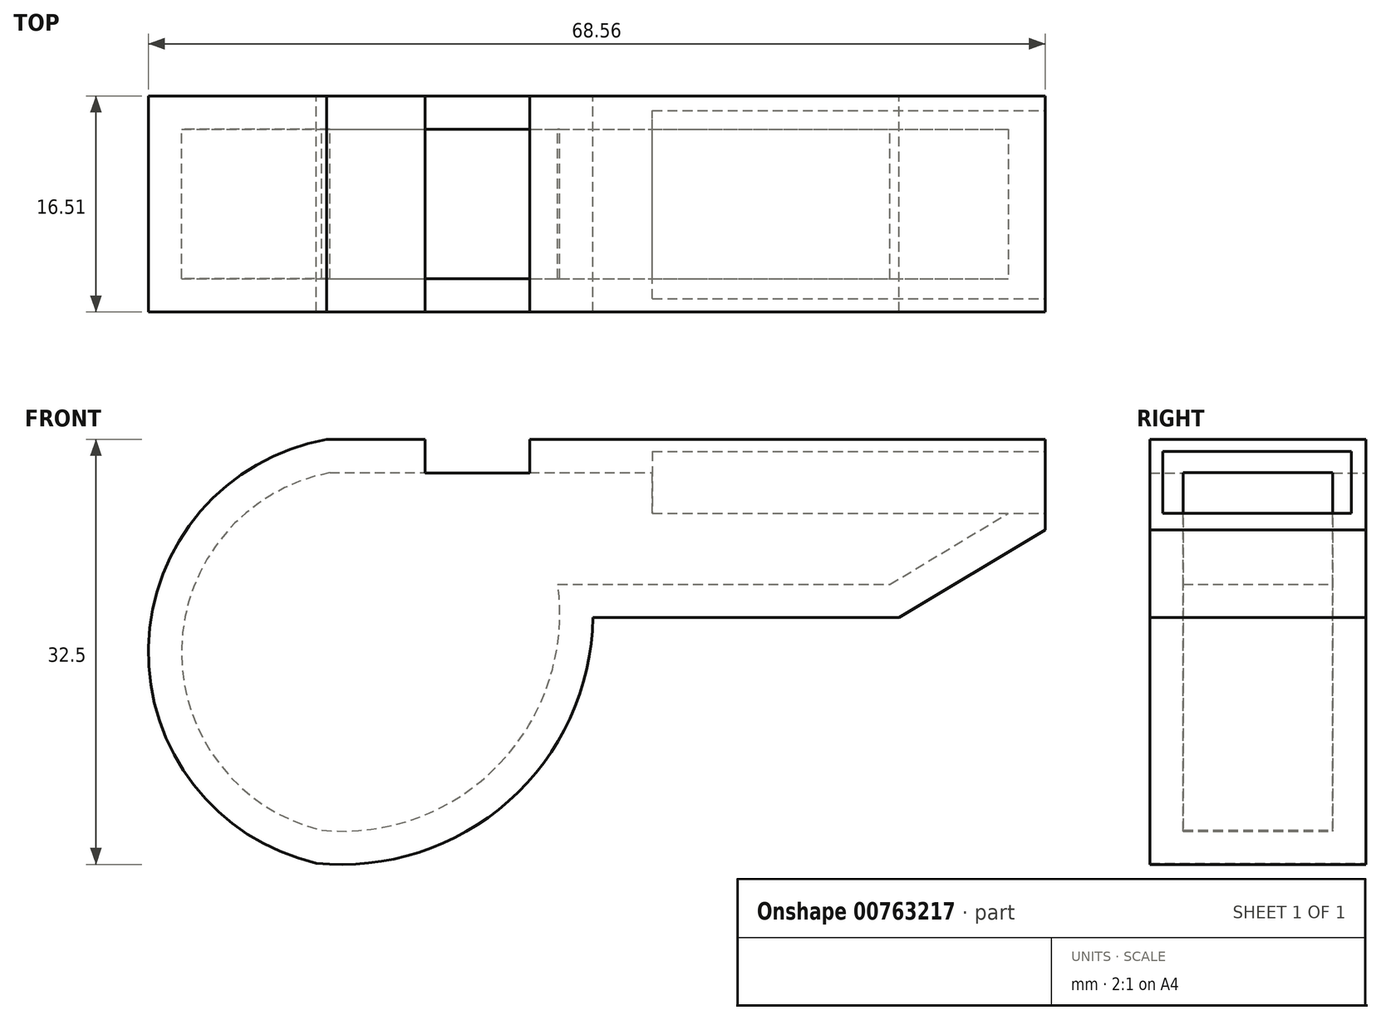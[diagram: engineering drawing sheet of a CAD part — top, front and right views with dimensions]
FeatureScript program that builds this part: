
annotation { "Feature Type Name" : "Feature", "Feature Type Description" : "" }
export const myFeature = defineFeature(function(context is Context, id is Id, definition is map)
    precondition{}
    {
        {
            var Q0;
            Q0=qCreatedBy(makeId("Front.planeOp"),FACE);
            var sketch = newSketch(context, id + "F0", { "sketchPlane" : qUnion([Q0])});
            skArc(sketch, "E0", {"start": v(-7.5, 23.6) * mm, "mid": v(-21.14, 7.73) * mm, "end": v(-8.3, -8.8) * mm});
            skLineSegment(sketch, "E1", {"start": v(-4.6, 23.6) * mm, "end": v(-7.5, 23.6) * mm});
            skLineSegment(sketch, "E2", {"start": v(-4.6, 23.6) * mm, "end": v(47.41, 23.6) * mm});
            skLineSegment(sketch, "E3", {"start": v(47.41, 23.6) * mm, "end": v(47.41, 16.7) * mm});
            skLineSegment(sketch, "E4", {"start": v(47.41, 16.7) * mm, "end": v(47.41, 9.98) * mm});
            skArc(sketch, "E5", {"start": v(-8.3, -8.8) * mm, "mid": v(6.4, -4.06) * mm, "end": v(12.84, 9.98) * mm});
            skLineSegment(sketch, "E6", {"start": v(12.84, 9.98) * mm, "end": v(36.23, 9.98) * mm});
            skLineSegment(sketch, "E7", {"start": v(36.23, 9.98) * mm, "end": v(47.41, 16.7) * mm});
            skSolve(sketch);
        }
        {
            var Q0;
            Q0=makeQuery(id+"F0.imprint","IMPRINT",FACE,{"disambiguationData":[TD([[makeQuery(id+"F0.imprint","IMPRINT",EDGE,{"derivedFrom":sQuery(id+"F0.wireOp",EDGE,"E0")}),1.0]])]});
            extrude(context, id + "F1", {"entities" : qUnion([Q0]), "depth" : 16.5 * mm, "offsetDistance" : 25.4 * mm});
        }
        {
            var Q0;
            Q0=makeQuery(id+"F1.opExtrude","CAP_FACE",FACE,{"disambiguationData":[OSD([sQuery(id+"F0.wireOp",EDGE,"E0"),sQuery(id+"F0.wireOp",EDGE,"E1"),sQuery(id+"F0.wireOp",EDGE,"E2"),sQuery(id+"F0.wireOp",EDGE,"E3"),sQuery(id+"F0.wireOp",EDGE,"E5"),sQuery(id+"F0.wireOp",EDGE,"E6"),sQuery(id+"F0.wireOp",EDGE,"E7")])],"isStart":false});
            var Q1;
            Q1=makeQuery(id+"F1.opExtrude","SWEPT_BODY",BODY,{"disambiguationData":[OSD([sQuery(id+"F0.wireOp",EDGE,"E0"),sQuery(id+"F0.wireOp",EDGE,"E1"),sQuery(id+"F0.wireOp",EDGE,"E2"),sQuery(id+"F0.wireOp",EDGE,"E3"),sQuery(id+"F0.wireOp",EDGE,"E5"),sQuery(id+"F0.wireOp",EDGE,"E6"),sQuery(id+"F0.wireOp",EDGE,"E7")])]});
            shell(context, id + "F2", {"isHollow" : true, "entities" : qUnion([Q0]), "parts" : qUnion([Q1]), "thickness" : 2.54 * mm});
        }
        {
            var Q0;
            Q0=makeQuery(id+"F1.opExtrude","SWEPT_FACE",FACE,{"disambiguationData":[OSD([sQuery(id+"F0.wireOp",EDGE,"E1"),sQuery(id+"F0.wireOp",EDGE,"E2")])]});
            var sketch = newSketch(context, id + "F3", { "sketchPlane" : qUnion([Q0])});
            skLineSegment(sketch, "E8", {"start": v(8, -16.51) * mm, "end": v(8, 0) * mm});
            skLineSegment(sketch, "E9", {"start": v(8, 0) * mm, "end": v(0, 0) * mm});
            skLineSegment(sketch, "E10", {"start": v(0, 0) * mm, "end": v(0, -16.51) * mm});
            skLineSegment(sketch, "E11", {"start": v(0, -16.51) * mm, "end": v(8, -16.51) * mm});
            skSolve(sketch);
        }
        {
            var Q0;
            Q0=makeQuery(id+"F3.imprint","IMPRINT",FACE,{"disambiguationData":[TD([[makeQuery(id+"F3.imprint","IMPRINT",EDGE,{"derivedFrom":sQuery(id+"F3.wireOp",EDGE,"E8")}),1.0]])]});
            extrude(context, id + "F4", {"entities" : qUnion([Q0]), "operationType" : NewBodyOperationType.REMOVE, "oppositeDirection" : true, "depth" : 2.3 * mm, "offsetDistance" : 25.4 * mm});
        }
        {
            var Q0;
            Q0=makeQuery(id+"F1.opExtrude","SWEPT_FACE",FACE,{"disambiguationData":[OSD([sQuery(id+"F0.wireOp",EDGE,"E3")])]});
            var sketch = newSketch(context, id + "F5", { "sketchPlane" : qUnion([Q0])});
            skLineSegment(sketch, "E12.bottom", {"start": v(-15.51, 22.7) * mm, "end": v(-1.1, 22.7) * mm});
            skLineSegment(sketch, "E12.top", {"start": v(-15.51, 17.96) * mm, "end": v(-1.1, 17.96) * mm});
            skLineSegment(sketch, "E12.left", {"start": v(-15.51, 22.7) * mm, "end": v(-15.51, 17.96) * mm});
            skLineSegment(sketch, "E12.right", {"start": v(-1.1, 22.7) * mm, "end": v(-1.1, 17.96) * mm});
            skSolve(sketch);
        }
        {
            var Q0;
            Q0=makeQuery(id+"F5.imprint","IMPRINT",FACE,{"disambiguationData":[TD([[makeQuery(id+"F5.imprint","IMPRINT",EDGE,{"derivedFrom":sQuery(id+"F5.wireOp",EDGE,"E12.bottom")}),-1.0]])]});
            extrude(context, id + "F6", {"entities" : qUnion([Q0]), "operationType" : NewBodyOperationType.REMOVE, "oppositeDirection" : true, "depth" : 30.02 * mm, "offsetDistance" : 25.4 * mm});
        }
        {
            var Q0;
            Q0=makeQuery(id+"F4.boolean.opBoolean","COPY",FACE,{"derivedFrom":makeQuery(id+"F4.opExtrude","CAP_FACE",FACE,{"disambiguationData":[OSD([sQuery(id+"F3.wireOp",EDGE,"E8"),sQuery(id+"F3.wireOp",EDGE,"E9"),sQuery(id+"F3.wireOp",EDGE,"E10"),sQuery(id+"F3.wireOp",EDGE,"E11")])],"isStart":false})});
            extrude(context, id + "F7", {"entities" : qUnion([Q0]), "operationType" : NewBodyOperationType.REMOVE, "oppositeDirection" : true, "depth" : 0.28 * mm, "offsetDistance" : 25.4 * mm});
        }
    });
